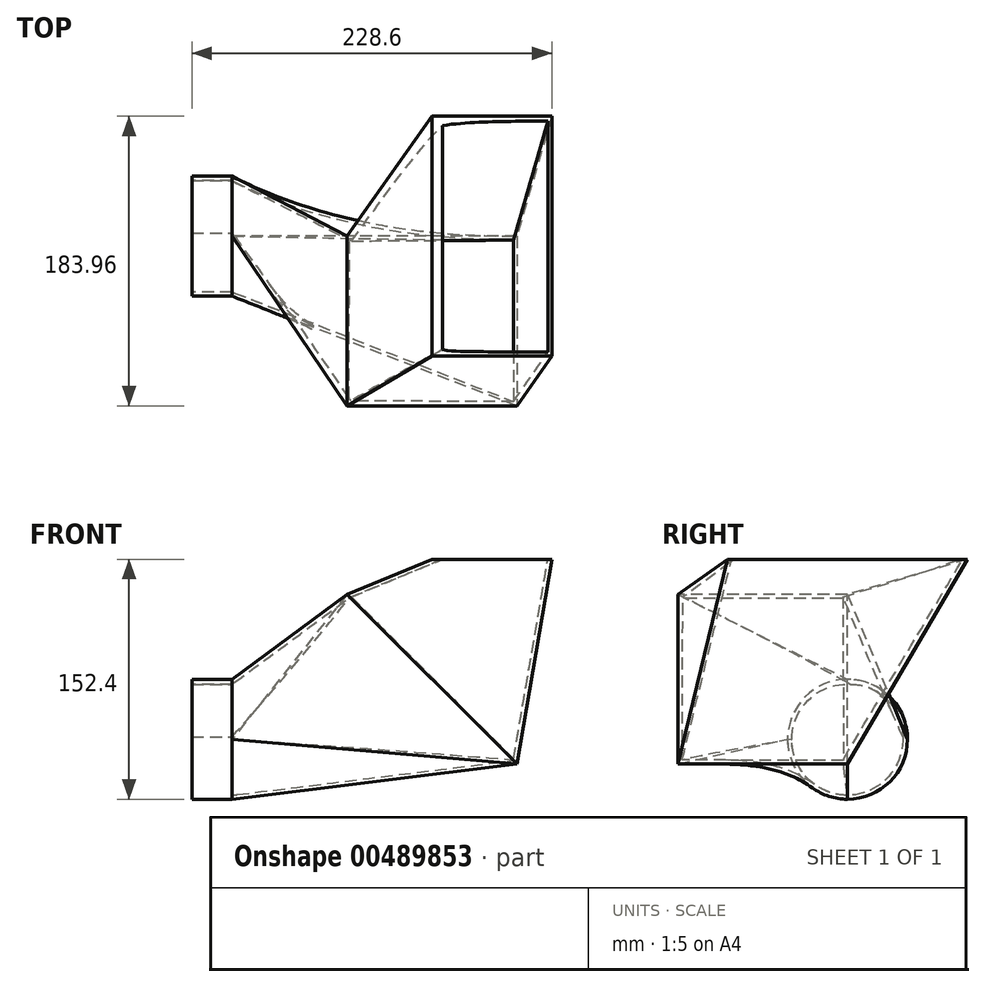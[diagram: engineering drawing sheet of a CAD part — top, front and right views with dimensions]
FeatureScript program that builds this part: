
annotation { "Feature Type Name" : "Feature", "Feature Type Description" : "" }
export const myFeature = defineFeature(function(context is Context, id is Id, definition is map)
    precondition{}
    {
        {
            var Q0;
            Q0=qCreatedBy(makeId("Front.planeOp"),FACE);
            var sketch = newSketch(context, id + "F0", { "sketchPlane" : qUnion([Q0])});
            skLineSegment(sketch, "E0", {"start": v(0, 76.2) * mm, "end": v(0, 0) * mm});
            skLineSegment(sketch, "E1", {"start": v(0, 0) * mm, "end": v(-127, 0) * mm});
            skLineSegment(sketch, "E2", {"start": v(-127, 0) * mm, "end": v(-152.4, 0) * mm});
            skLineSegment(sketch, "E3", {"start": v(76.2, 76.2) * mm, "end": v(0, 0) * mm});
            skSolve(sketch);
        }
        {
            var Q0;
            Q0=sQuery(id+"F0.wireOp",VERTEX,"E0.start");
            var Q1;
            Q1=sQuery(id+"F0.wireOp",EDGE,"E0");
            cPlane(context, id + "F1", {"entities" : qUnion([Q0, Q1]), "cplaneType" : CPlaneType.LINE_POINT, "offset" : 25.4 * mm, "width" : 152.4 * mm, "height" : 152.4 * mm});
        }
        {
            var Q0;
            Q0=sQuery(id+"F0.wireOp",EDGE,"E3");
            var Q1;
            Q1=sQuery(id+"F0.wireOp",VERTEX,"E1.start");
            cPlane(context, id + "F2", {"entities" : qUnion([Q0, Q1]), "cplaneType" : CPlaneType.LINE_POINT, "offset" : 25.4 * mm, "width" : 152.4 * mm, "height" : 152.4 * mm});
        }
        {
            var Q0;
            Q0=sQuery(id+"F0.wireOp",VERTEX,"E2.start");
            var Q1;
            Q1=qCreatedBy(makeId("Right.planeOp"),FACE);
            cPlane(context, id + "F3", {"entities" : qUnion([Q0, Q1]), "cplaneType" : CPlaneType.PLANE_POINT, "offset" : 25.4 * mm, "width" : 152.4 * mm, "height" : 152.4 * mm});
        }
        {
            var Q0;
            Q0=qCreatedBy(id+"F1.planeOp",FACE);
            var sketch = newSketch(context, id + "F4", { "sketchPlane" : qUnion([Q0])});
            skLineSegment(sketch, "E4.bottom", {"start": v(0, -76.2) * mm, "end": v(76.2, -76.2) * mm});
            skLineSegment(sketch, "E4.top", {"start": v(0, 76.2) * mm, "end": v(76.2, 76.2) * mm});
            skLineSegment(sketch, "E4.left", {"start": v(0, -76.2) * mm, "end": v(0, 76.2) * mm});
            skLineSegment(sketch, "E4.right", {"start": v(76.2, -76.2) * mm, "end": v(76.2, 76.2) * mm});
            skSolve(sketch);
        }
        {
            var Q0;
            Q0=qCreatedBy(id+"F2.planeOp",FACE);
            var sketch = newSketch(context, id + "F5", { "sketchPlane" : qUnion([Q0])});
            skLineSegment(sketch, "E5.bottom", {"start": v(0, -76.2) * mm, "end": v(107.76, -76.2) * mm});
            skLineSegment(sketch, "E5.top", {"start": v(0, 76.2) * mm, "end": v(107.76, 76.2) * mm});
            skLineSegment(sketch, "E5.left", {"start": v(0, -76.2) * mm, "end": v(0, 76.2) * mm});
            skLineSegment(sketch, "E5.right", {"start": v(107.76, -76.2) * mm, "end": v(107.76, 76.2) * mm});
            skSolve(sketch);
        }
        {
            var Q0;
            Q0=qCreatedBy(id+"F3.planeOp",FACE);
            var sketch = newSketch(context, id + "F6", { "sketchPlane" : qUnion([Q0])});
            skCircle(sketch, "E6", {"center": v(0, -38.1) * mm, "radius": 38.1 * mm});
            skSolve(sketch);
        }
        {
            var Q0;
            Q0=makeQuery(id+"F4.imprint","IMPRINT",FACE,{"disambiguationData":[TD([[makeQuery(id+"F4.imprint","IMPRINT",EDGE,{"derivedFrom":sQuery(id+"F4.wireOp",EDGE,"E4.bottom")}),1.0]])]});
            var Q1;
            Q1=makeQuery(id+"F5.imprint","IMPRINT",FACE,{"disambiguationData":[TD([[makeQuery(id+"F5.imprint","IMPRINT",EDGE,{"derivedFrom":sQuery(id+"F5.wireOp",EDGE,"E5.bottom")}),1.0]])]});
            loft(context, id + "F7", {"sheetProfilesArray" : [{ "sheetProfileEntities" : qUnion([Q0]) }, { "sheetProfileEntities" : qUnion([Q1]) }]});
        }
        {
            var Q1;
            Q1=makeQuery(id+"F7.opLoft","CAP_FACE",FACE,{"disambiguationData":[OSD([makeQuery(id+"F5.imprint","IMPRINT",FACE,{"disambiguationData":[TD([[makeQuery(id+"F5.imprint","IMPRINT",EDGE,{"derivedFrom":sQuery(id+"F5.wireOp",EDGE,"E5.bottom")}),1.0]])]})])],"isStart":true});
            var Q2;
            Q2=makeQuery(id+"F6.imprint","IMPRINT",FACE,{"disambiguationData":[TD([[makeQuery(id+"F6.imprint","IMPRINT",EDGE,{"derivedFrom":sQuery(id+"F6.wireOp",EDGE,"E6")}),1.0]])]});
            loft(context, id + "F8", {"operationType" : NewBodyOperationType.ADD, "sheetProfilesArray" : [{ "sheetProfileEntities" : qUnion([Q1]) }, { "sheetProfileEntities" : qUnion([Q2]) }]});
        }
        {
            var Q0;
            Q0=makeQuery(id+"F7.opLoft","CAP_FACE",FACE,{"disambiguationData":[OSD([makeQuery(id+"F4.imprint","IMPRINT",FACE,{"disambiguationData":[TD([[makeQuery(id+"F4.imprint","IMPRINT",EDGE,{"derivedFrom":sQuery(id+"F4.wireOp",EDGE,"E4.bottom")}),1.0]])]})])],"isStart":true});
            var Q1;
            Q1=makeQuery(id+"F8.opLoft","CAP_FACE",FACE,{"disambiguationData":[OSD([makeQuery(id+"F6.imprint","IMPRINT",FACE,{"disambiguationData":[TD([[makeQuery(id+"F6.imprint","IMPRINT",EDGE,{"derivedFrom":sQuery(id+"F6.wireOp",EDGE,"E6")}),1.0]])]})])],"isStart":true});
            shell(context, id + "F9", {"entities" : qUnion([Q0, Q1]), "thickness" : 2.54 * mm});
        }
        {
            var Q0;
            Q0=makeQuery(id+"F8.opLoft","CAP_FACE",FACE,{"disambiguationData":[OSD([makeQuery(id+"F6.imprint","IMPRINT",FACE,{"disambiguationData":[TD([[makeQuery(id+"F6.imprint","IMPRINT",EDGE,{"derivedFrom":sQuery(id+"F6.wireOp",EDGE,"E6")}),1.0]])]})])],"isStart":true});
            extrude(context, id + "F10", {"entities" : qUnion([Q0]), "operationType" : NewBodyOperationType.ADD, "depth" : 25.4 * mm});
        }
    });
